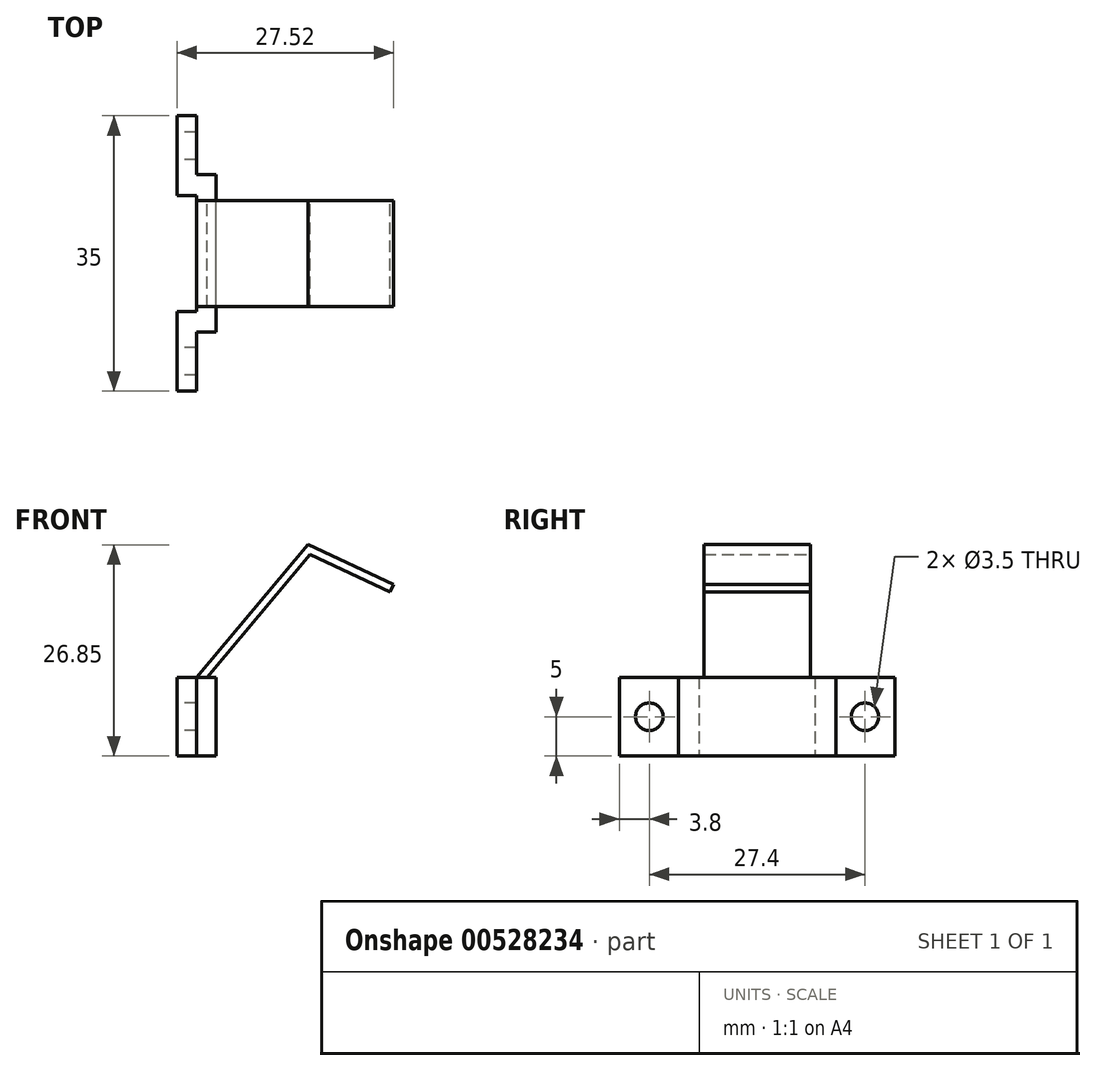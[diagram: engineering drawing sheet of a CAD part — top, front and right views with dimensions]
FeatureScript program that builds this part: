
annotation { "Feature Type Name" : "Feature", "Feature Type Description" : "" }
export const myFeature = defineFeature(function(context is Context, id is Id, definition is map)
    precondition{}
    {
        {
            var Q0;
            Q0=qCreatedBy(makeId("Front.planeOp"),FACE);
            var sketch = newSketch(context, id + "F0", { "sketchPlane" : qUnion([Q0])});
            skLineSegment(sketch, "E0.bottom", {"start": v(1.25, 5) * mm, "end": v(-1.25, 5) * mm});
            skLineSegment(sketch, "E0.top", {"start": v(1.25, -5) * mm, "end": v(-1.25, -5) * mm});
            skLineSegment(sketch, "E0.left", {"start": v(1.25, 5) * mm, "end": v(1.25, -5) * mm});
            skLineSegment(sketch, "E0.right", {"start": v(-1.25, 5) * mm, "end": v(-1.25, -5) * mm});
            skPoint(sketch, "E0.middle", {"position": v(0, 0) * mm});
            skLineSegment(sketch, "E1", {"start": v(-1.25, 5) * mm, "end": v(-1.25, -13.91) * mm, "construction": true});
            skLineSegment(sketch, "E2", {"start": v(-1.25, -13.91) * mm, "end": v(-1.25, 20.21) * mm, "construction": true});
            skLineSegment(sketch, "E3.MirrorCS", {"start": v(-3.75, 5) * mm, "end": v(-1.25, 5) * mm});
            skLineSegment(sketch, "E4.MirrorCS", {"start": v(-3.75, 5) * mm, "end": v(-3.75, -5) * mm});
            skLineSegment(sketch, "E5.MirrorCS", {"start": v(-3.75, -5) * mm, "end": v(-1.25, -5) * mm});
            skLineSegment(sketch, "E6", {"start": v(-1.25, 5) * mm, "end": v(12.9, 21.85) * mm});
            skLineSegment(sketch, "E7", {"start": v(12.9, 21.85) * mm, "end": v(23.77, 16.78) * mm});
            skLineSegment(sketch, "E8.0", {"start": v(0.06, 5) * mm, "end": v(13.16, 20.62) * mm});
            skLineSegment(sketch, "E9.0", {"start": v(13.16, 20.62) * mm, "end": v(23.34, 15.88) * mm});
            skLineSegment(sketch, "E10", {"start": v(23.34, 15.88) * mm, "end": v(23.77, 16.78) * mm});
            skSolve(sketch);
        }
        {
            var Q0;
            Q0=makeQuery(id+"F0.imprint","IMPRINT",FACE,{"disambiguationData":[TD([[makeQuery(id+"F0.imprint","IMPRINT",EDGE,{"derivedFrom":sQuery(id+"F0.wireOp",EDGE,"E0.bottom")}),1.0]])]});
            extrude(context, id + "F1", {"entities" : qUnion([Q0]), "endBound" : BoundingType.SYMMETRIC, "depth" : 20 * mm, "offsetDistance" : 25 * mm});
        }
        {
            var Q0;
            Q0=makeQuery(id+"F0.imprint","IMPRINT",FACE,{"disambiguationData":[TD([[makeQuery(id+"F0.imprint","IMPRINT",EDGE,{"derivedFrom":sQuery(id+"F0.wireOp",EDGE,"E0.bottom")}),-1.0]])]});
            extrude(context, id + "F2", {"entities" : qUnion([Q0]), "operationType" : NewBodyOperationType.ADD, "endBound" : BoundingType.SYMMETRIC, "depth" : 13.5 * mm, "offsetDistance" : 25 * mm});
        }
        {
            var Q0;
            Q0=makeQuery(id+"F0.imprint","IMPRINT",FACE,{"disambiguationData":[TD([[makeQuery(id+"F0.imprint","IMPRINT",EDGE,{"derivedFrom":sQuery(id+"F0.wireOp",EDGE,"E0.right")}),-1.0]])]});
            extrude(context, id + "F3", {"entities" : qUnion([Q0]), "operationType" : NewBodyOperationType.ADD, "endBound" : BoundingType.SYMMETRIC, "depth" : 35 * mm, "offsetDistance" : 25 * mm});
        }
        {
            var Q0;
            Q0=makeQuery(id+"F0.imprint","IMPRINT",FACE,{"disambiguationData":[TD([[makeQuery(id+"F0.imprint","IMPRINT",EDGE,{"derivedFrom":sQuery(id+"F0.wireOp",EDGE,"E0.right")}),-1.0]])]});
            extrude(context, id + "F4", {"entities" : qUnion([Q0]), "operationType" : NewBodyOperationType.REMOVE, "endBound" : BoundingType.SYMMETRIC, "depth" : 14.75 * mm, "offsetDistance" : 25 * mm});
        }
        {
            var Q0;
            Q0=qCreatedBy(makeId("Right.planeOp"),FACE);
            var sketch = newSketch(context, id + "F5", { "sketchPlane" : qUnion([Q0])});
            skCircle(sketch, "E11", {"center": v(-13.7, 0) * mm, "radius": 1.75 * mm});
            skLineSegment(sketch, "E12", {"start": v(0, 14.16) * mm, "end": v(0, -7.71) * mm, "construction": true});
            skCircle(sketch, "E13.MirrorC", {"center": v(13.7, 0) * mm, "radius": 1.75 * mm});
            skSolve(sketch);
        }
        {
            var Q0;
            Q0 = qSketchRegion(id + "F5", true);
            extrude(context, id + "F6", {"entities" : qUnion([Q0]), "operationType" : NewBodyOperationType.REMOVE, "endBound" : BoundingType.SYMMETRIC, "depth" : 10 * mm, "offsetDistance" : 25 * mm});
        }
    });
